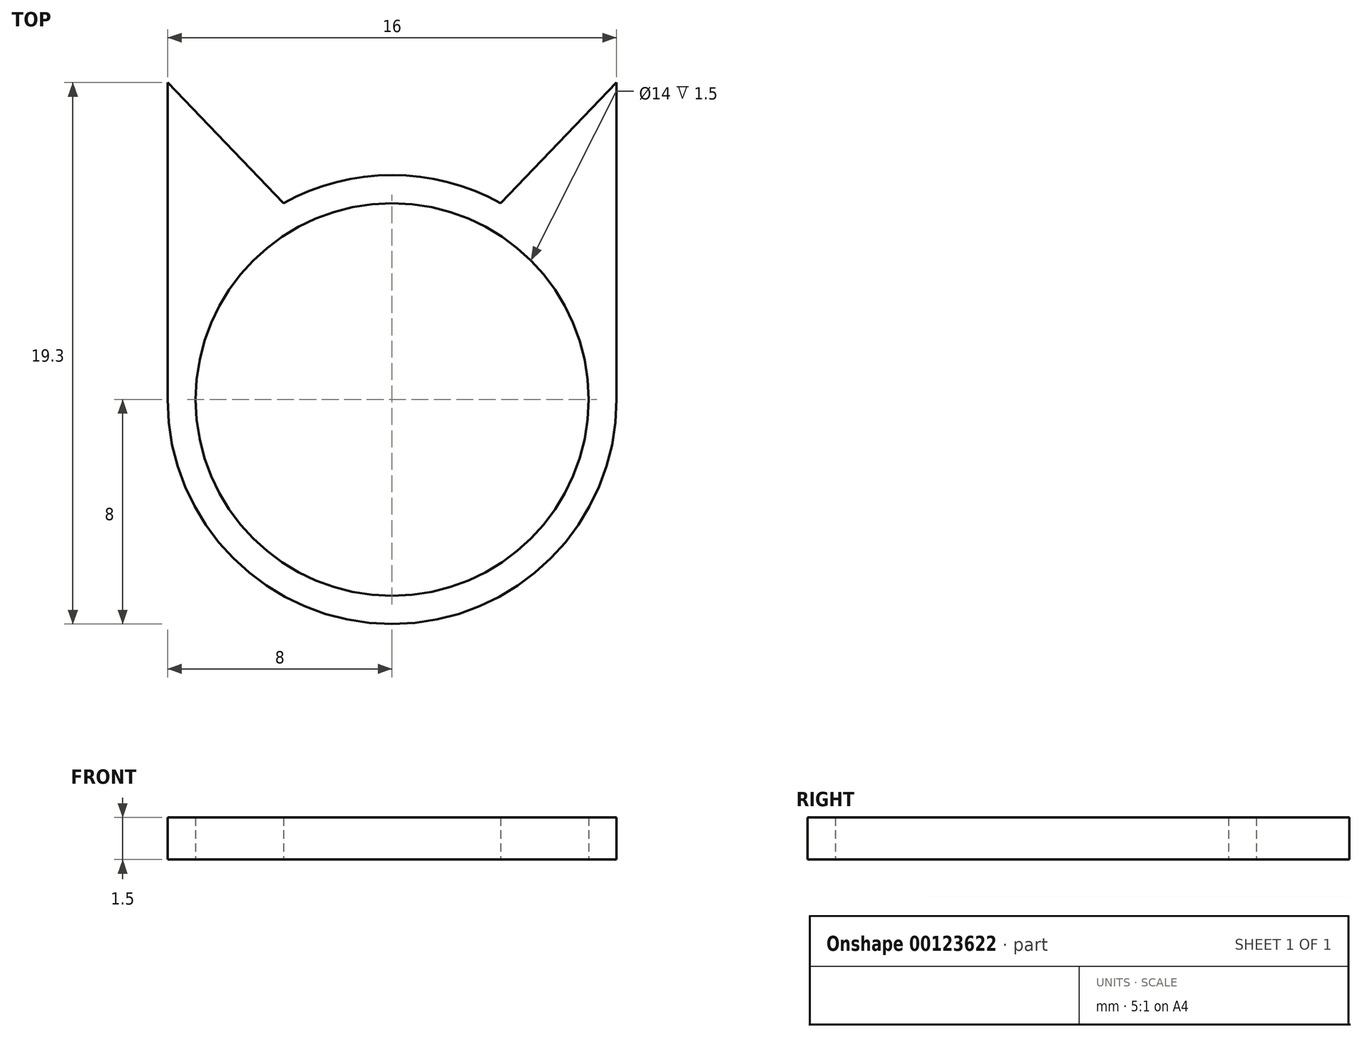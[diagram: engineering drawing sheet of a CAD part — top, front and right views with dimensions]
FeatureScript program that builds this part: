
annotation { "Feature Type Name" : "Feature", "Feature Type Description" : "" }
export const myFeature = defineFeature(function(context is Context, id is Id, definition is map)
    precondition{}
    {
        {
            var Q0;
            Q0=qCreatedBy(makeId("Top.planeOp"),FACE);
            var sketch = newSketch(context, id + "F0", { "sketchPlane" : qUnion([Q0])});
            skCircle(sketch, "E0", {"center": v(0, 0) * mm, "radius": 7 * mm});
            skCircle(sketch, "E1", {"center": v(0, 0) * mm, "radius": 8 * mm});
            skLineSegment(sketch, "E2", {"start": v(-8, 0) * mm, "end": v(-8, 11.3) * mm});
            skLineSegment(sketch, "E3", {"start": v(-8, 11.3) * mm, "end": v(-3.87, 7) * mm});
            skLineSegment(sketch, "E4.MirrorCS", {"start": v(8, 0) * mm, "end": v(8, 11.3) * mm});
            skLineSegment(sketch, "E5.MirrorCS", {"start": v(8, 11.3) * mm, "end": v(3.87, 7) * mm});
            skSolve(sketch);
        }
        {
            var Q0;
            Q0 = qSketchRegion(id + "F0", true);
            extrude(context, id + "F1", {"entities" : qUnion([Q0]), "depth" : 1.5 * mm});
        }
    });
